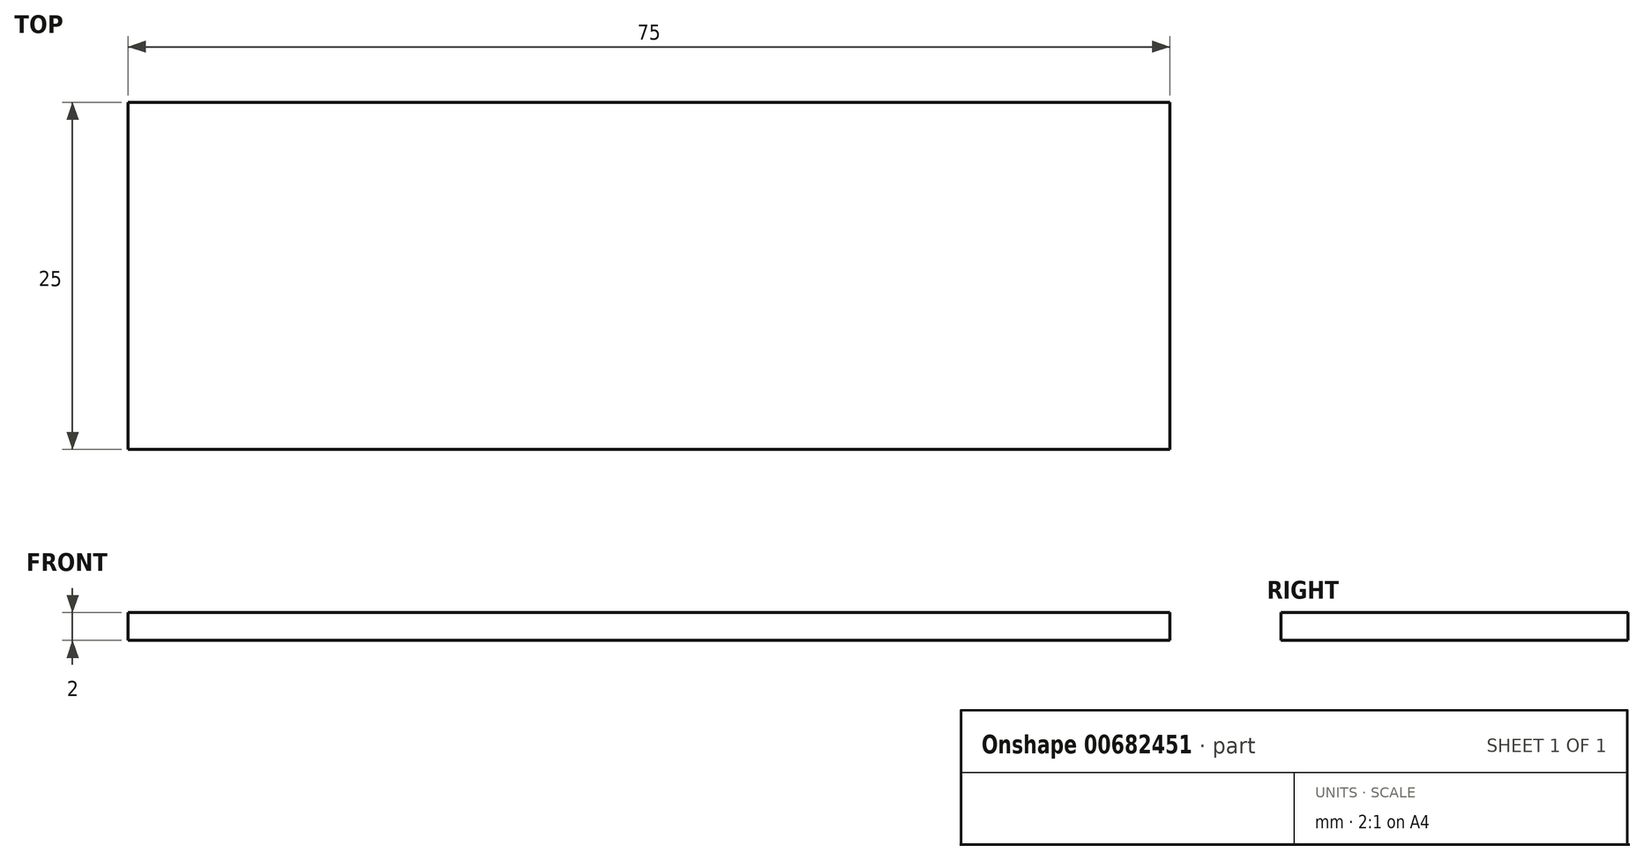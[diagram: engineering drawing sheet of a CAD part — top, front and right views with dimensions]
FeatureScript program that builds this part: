
annotation { "Feature Type Name" : "Feature", "Feature Type Description" : "" }
export const myFeature = defineFeature(function(context is Context, id is Id, definition is map)
    precondition{}
    {
        {
            var Q0;
            Q0=qCreatedBy(makeId("Top.planeOp"),FACE);
            var sketch = newSketch(context, id + "F0", { "sketchPlane" : qUnion([Q0])});
            skLineSegment(sketch, "E0.bottom", {"start": v(-37.5, 12.5) * mm, "end": v(37.5, 12.5) * mm});
            skLineSegment(sketch, "E0.top", {"start": v(-37.5, -12.5) * mm, "end": v(37.5, -12.5) * mm});
            skLineSegment(sketch, "E0.left", {"start": v(-37.5, 12.5) * mm, "end": v(-37.5, -12.5) * mm});
            skLineSegment(sketch, "E0.right", {"start": v(37.5, 12.5) * mm, "end": v(37.5, -12.5) * mm});
            skPoint(sketch, "E0.middle", {"position": v(0, 0) * mm});
            skPoint(sketch, "E1", {"position": v(-37.5, 12.5) * mm});
            skSolve(sketch);
        }
        {
            var Q0;
            Q0=makeQuery(id+"F0.imprint","IMPRINT",FACE,{"disambiguationData":[TD([[makeQuery(id+"F0.imprint","IMPRINT",EDGE,{"derivedFrom":sQuery(id+"F0.wireOp",EDGE,"E0.bottom")}),-1.0]])]});
            extrude(context, id + "F1", {"entities" : qUnion([Q0]), "depth" : 2 * mm, "offsetDistance" : 25.4 * mm});
        }
    });
